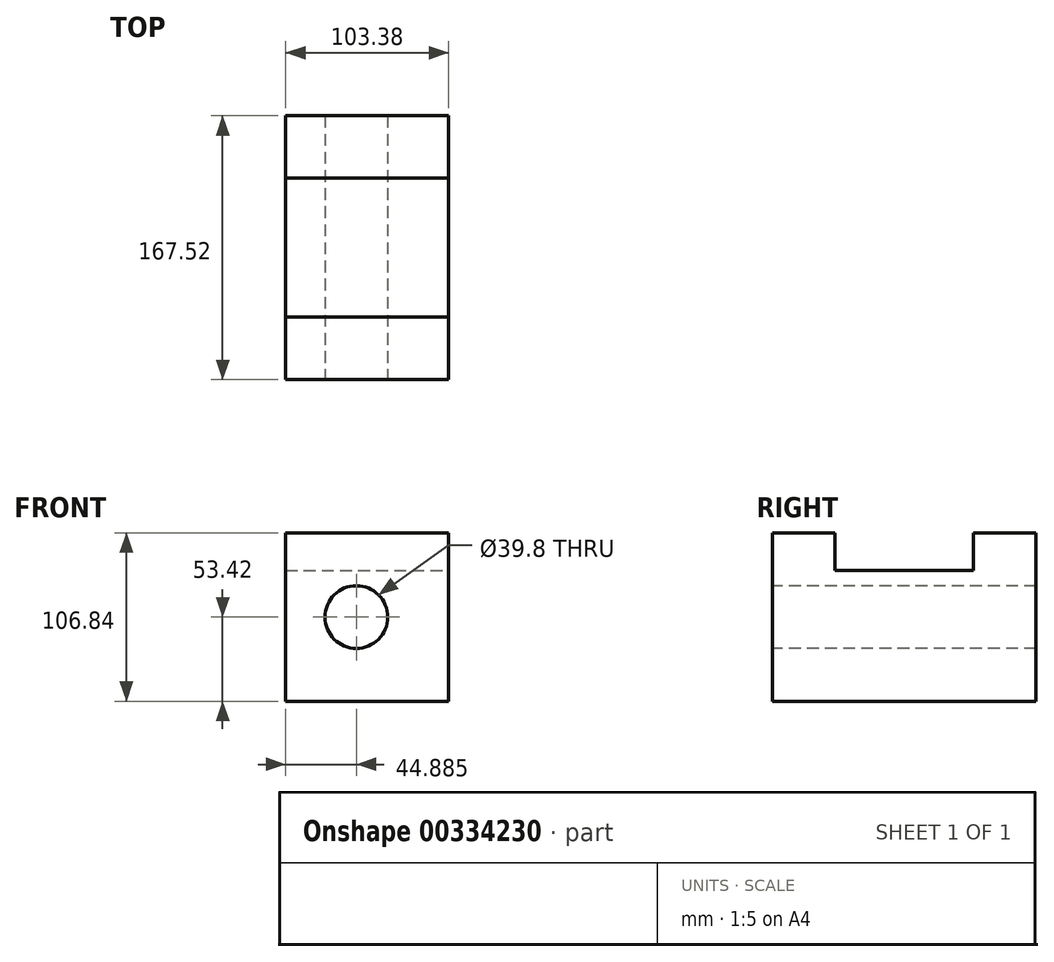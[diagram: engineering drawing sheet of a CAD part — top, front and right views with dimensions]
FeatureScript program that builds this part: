
annotation { "Feature Type Name" : "Feature", "Feature Type Description" : "" }
export const myFeature = defineFeature(function(context is Context, id is Id, definition is map)
    precondition{}
    {
        {
            var Q0;
            Q0=qCreatedBy(makeId("Right.planeOp"),FACE);
            var sketch = newSketch(context, id + "F0", { "sketchPlane" : qUnion([Q0])});
            skLineSegment(sketch, "E0.bottom", {"start": v(83.76, 53.42) * mm, "end": v(-83.76, 53.42) * mm});
            skLineSegment(sketch, "E0.top", {"start": v(83.76, -53.42) * mm, "end": v(-83.76, -53.42) * mm});
            skLineSegment(sketch, "E0.left", {"start": v(83.76, 53.42) * mm, "end": v(83.76, -53.42) * mm});
            skLineSegment(sketch, "E0.right", {"start": v(-83.76, 53.42) * mm, "end": v(-83.76, -53.42) * mm});
            skPoint(sketch, "E0.middle", {"position": v(0, 0) * mm});
            skSolve(sketch);
        }
        {
            var Q0;
            Q0 = qSketchRegion(id + "F0", true);
            extrude(context, id + "F1", {"entities" : qUnion([Q0]), "depth" : 103.38 * mm});
        }
        {
            var Q0;
            Q0=makeQuery(id+"F1.opExtrude","SWEPT_FACE",FACE,{"disambiguationData":[OSD([sQuery(id+"F0.wireOp",EDGE,"E0.right")])]});
            var sketch = newSketch(context, id + "F2", { "sketchPlane" : qUnion([Q0])});
            skCircle(sketch, "E1", {"center": v(44.89, 0) * mm, "radius": 19.9 * mm});
            skSolve(sketch);
        }
        {
            var Q0;
            Q0 = qSketchRegion(id + "F2", true);
            extrude(context, id + "F3", {"entities" : qUnion([Q0]), "operationType" : NewBodyOperationType.REMOVE, "oppositeDirection" : true, "depth" : 229.36 * mm});
        }
        {
            var Q0;
            Q0=makeQuery(id+"F1.opExtrude","CAP_FACE",FACE,{"disambiguationData":[OSD([sQuery(id+"F0.wireOp",EDGE,"E0.bottom"),sQuery(id+"F0.wireOp",EDGE,"E0.top"),sQuery(id+"F0.wireOp",EDGE,"E0.left"),sQuery(id+"F0.wireOp",EDGE,"E0.right")])],"isStart":false});
            var sketch = newSketch(context, id + "F4", { "sketchPlane" : qUnion([Q0])});
            skLineSegment(sketch, "E2.bottom", {"start": v(-44.06, 29.73) * mm, "end": v(44.06, 29.73) * mm});
            skLineSegment(sketch, "E2.top", {"start": v(-44.06, 77.1) * mm, "end": v(44.06, 77.1) * mm});
            skLineSegment(sketch, "E2.left", {"start": v(-44.06, 29.73) * mm, "end": v(-44.06, 77.1) * mm});
            skLineSegment(sketch, "E2.right", {"start": v(44.06, 29.73) * mm, "end": v(44.06, 77.1) * mm});
            skPoint(sketch, "E2.middle", {"position": v(0, 53.42) * mm});
            skSolve(sketch);
        }
        {
            var Q0;
            Q0 = qSketchRegion(id + "F4", true);
            extrude(context, id + "F5", {"entities" : qUnion([Q0]), "operationType" : NewBodyOperationType.REMOVE, "oppositeDirection" : true, "depth" : 133.1 * mm});
        }
    });
